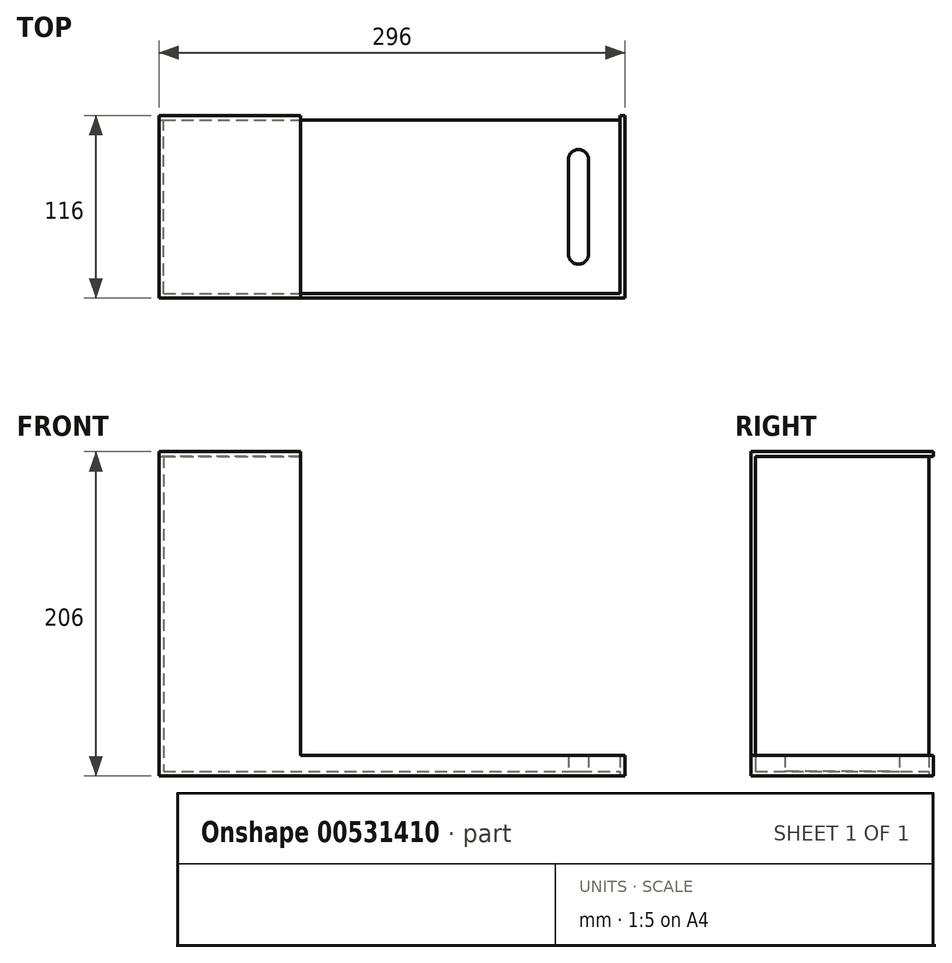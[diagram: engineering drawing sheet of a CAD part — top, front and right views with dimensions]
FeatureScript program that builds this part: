
annotation { "Feature Type Name" : "Feature", "Feature Type Description" : "" }
export const myFeature = defineFeature(function(context is Context, id is Id, definition is map)
    precondition{}
    {
        {
            var Q0;
            Q0=qCreatedBy(makeId("Front.planeOp"),FACE);
            var sketch = newSketch(context, id + "F0", { "sketchPlane" : qUnion([Q0])});
            skLineSegment(sketch, "E0", {"start": v(-49.76, 0) * mm, "end": v(-49.76, 203) * mm});
            skLineSegment(sketch, "E1", {"start": v(-49.76, 203) * mm, "end": v(-46.76, 203) * mm});
            skLineSegment(sketch, "E2", {"start": v(-46.76, 203) * mm, "end": v(-46.76, 3) * mm});
            skLineSegment(sketch, "E3", {"start": v(-46.76, 3) * mm, "end": v(243.24, 3) * mm});
            skLineSegment(sketch, "E4", {"start": v(243.24, 3) * mm, "end": v(243.24, 0) * mm});
            skLineSegment(sketch, "E5", {"start": v(243.24, 0) * mm, "end": v(-49.76, 0) * mm});
            skSolve(sketch);
        }
        {
            var Q0;
            Q0 = qSketchRegion(id + "F0", true);
            extrude(context, id + "F1", {"entities" : qUnion([Q0]), "depth" : 55 * mm, "offsetDistance" : 25 * mm, "hasSecondDirection" : true, "secondDirectionOppositeDirection" : true, "secondDirectionDepth" : 55 * mm});
        }
        {
            var Q0;
            Q0=makeQuery(id+"F1.opExtrude","CAP_FACE",FACE,{"disambiguationData":[OSD([sQuery(id+"F0.wireOp",EDGE,"E0"),sQuery(id+"F0.wireOp",EDGE,"E1"),sQuery(id+"F0.wireOp",EDGE,"E2"),sQuery(id+"F0.wireOp",EDGE,"E3"),sQuery(id+"F0.wireOp",EDGE,"E4"),sQuery(id+"F0.wireOp",EDGE,"E5")])],"isStart":false});
            cPlane(context, id + "F2", {"entities" : qUnion([Q0]), "cplaneType" : CPlaneType.OFFSET, "offset" : 0 * mm, "width" : 150 * mm, "height" : 150 * mm});
        }
        {
            var Q0;
            Q0=qCreatedBy(id+"F2.planeOp",FACE);
            var sketch = newSketch(context, id + "F3", { "sketchPlane" : qUnion([Q0])});
            skLineSegment(sketch, "E6.0", {"start": v(-49.76, 0) * mm, "end": v(-49.76, 203) * mm, "construction": true});
            skLineSegment(sketch, "E7.0", {"start": v(243.24, 0) * mm, "end": v(-49.76, 0) * mm, "construction": true});
            skLineSegment(sketch, "E8.bottom", {"start": v(-49.76, 203) * mm, "end": v(40.24, 203) * mm});
            skLineSegment(sketch, "E8.top", {"start": v(-49.76, 0) * mm, "end": v(243.24, 0) * mm});
            skLineSegment(sketch, "E8.left", {"start": v(-49.76, 203) * mm, "end": v(-49.76, 0) * mm});
            skLineSegment(sketch, "E8.right", {"start": v(243.24, 13) * mm, "end": v(243.24, 0) * mm});
            skLineSegment(sketch, "E9", {"start": v(40.24, 203) * mm, "end": v(40.24, 13) * mm});
            skLineSegment(sketch, "E10", {"start": v(40.24, 13) * mm, "end": v(243.24, 13) * mm});
            skSolve(sketch);
        }
        {
            var Q0;
            Q0 = qSketchRegion(id + "F3", true);
            extrude(context, id + "F4", {"entities" : qUnion([Q0]), "operationType" : NewBodyOperationType.ADD, "depth" : 3 * mm, "offsetDistance" : 25 * mm});
        }
        {
            var Q0;
            {var subQ0=sQuery(id+"F3.wireOp",EDGE,"E8.bottom");Q0=makeQuery(id+"FY8N2gA1KWKEWoe_1.1.F4.boolean.opBoolean","MERGE",FACE,{"derivedFrom":[makeQuery(id+"F4.boolean.opBoolean","MERGE",FACE,{"derivedFrom":[makeQuery(id+"F1.opExtrude","SWEPT_FACE",FACE,{"disambiguationData":[OSD([sQuery(id+"F0.wireOp",EDGE,"E1")])]}),makeQuery(id+"F4.opExtrude","SWEPT_FACE",FACE,{"disambiguationData":[OSD([subQ0])]})]}),makeQuery(id+"FY8N2gA1KWKEWoe_1.1.F4.opExtrude","SWEPT_FACE",FACE,{"disambiguationData":[OSD([subQ0])]})]});}
            cPlane(context, id + "F5", {"entities" : qUnion([Q0]), "cplaneType" : CPlaneType.OFFSET, "offset" : 0 * mm, "width" : 150 * mm, "height" : 150 * mm});
        }
        {
            var Q0;
            Q0=qCreatedBy(id+"F5.planeOp",FACE);
            var sketch = newSketch(context, id + "F6", { "sketchPlane" : qUnion([Q0])});
            skLineSegment(sketch, "E11.0", {"start": v(-49.76, 58) * mm, "end": v(40.24, 58) * mm, "construction": true});
            skLineSegment(sketch, "E12.0", {"start": v(-49.76, -58) * mm, "end": v(-49.76, 58) * mm, "construction": true});
            skLineSegment(sketch, "E13.bottom", {"start": v(40.24, 58) * mm, "end": v(-49.76, 58) * mm});
            skLineSegment(sketch, "E13.top", {"start": v(40.24, -58) * mm, "end": v(-49.76, -58) * mm});
            skLineSegment(sketch, "E13.left", {"start": v(40.24, 58) * mm, "end": v(40.24, -58) * mm});
            skLineSegment(sketch, "E13.right", {"start": v(-49.76, 58) * mm, "end": v(-49.76, -58) * mm});
            skSolve(sketch);
        }
        {
            var Q0;
            Q0 = qSketchRegion(id + "F6", true);
            extrude(context, id + "F7", {"entities" : qUnion([Q0]), "operationType" : NewBodyOperationType.ADD, "depth" : 3 * mm, "offsetDistance" : 25 * mm});
        }
        {
            var Q0;
            {var subQ0=sQuery(id+"F3.wireOp",EDGE,"E8.right");Q0=makeQuery(id+"FY8N2gA1KWKEWoe_1.1.F4.boolean.opBoolean","MERGE",FACE,{"derivedFrom":[makeQuery(id+"F4.boolean.opBoolean","MERGE",FACE,{"derivedFrom":[makeQuery(id+"F1.opExtrude","SWEPT_FACE",FACE,{"disambiguationData":[OSD([sQuery(id+"F0.wireOp",EDGE,"E4")])]}),makeQuery(id+"F4.opExtrude","SWEPT_FACE",FACE,{"disambiguationData":[OSD([subQ0])]})]}),makeQuery(id+"FY8N2gA1KWKEWoe_1.1.F4.opExtrude","SWEPT_FACE",FACE,{"disambiguationData":[OSD([subQ0])]})]});}
            cPlane(context, id + "F8", {"entities" : qUnion([Q0]), "cplaneType" : CPlaneType.OFFSET, "offset" : 0 * mm, "width" : 150 * mm, "height" : 150 * mm});
        }
        {
            var Q0;
            Q0=qCreatedBy(id+"F8.planeOp",FACE);
            var sketch = newSketch(context, id + "F9", { "sketchPlane" : qUnion([Q0])});
            skLineSegment(sketch, "E14.0", {"start": v(-58, 13) * mm, "end": v(-58, 0) * mm, "construction": true});
            skLineSegment(sketch, "E15.0", {"start": v(-58, 0) * mm, "end": v(58, 0) * mm, "construction": true});
            skLineSegment(sketch, "E16.bottom", {"start": v(-58, 13) * mm, "end": v(58, 13) * mm});
            skLineSegment(sketch, "E16.top", {"start": v(-58, 0) * mm, "end": v(58, 0) * mm});
            skLineSegment(sketch, "E16.left", {"start": v(-58, 13) * mm, "end": v(-58, 0) * mm});
            skLineSegment(sketch, "E16.right", {"start": v(58, 13) * mm, "end": v(58, 0) * mm});
            skSolve(sketch);
        }
        {
            var Q0;
            Q0 = qSketchRegion(id + "F9", true);
            extrude(context, id + "F10", {"entities" : qUnion([Q0]), "operationType" : NewBodyOperationType.ADD, "depth" : 3 * mm, "offsetDistance" : 25 * mm});
        }
        {
            var Q0;
            Q0=makeQuery(id+"F1.opExtrude","SWEPT_FACE",FACE,{"disambiguationData":[OSD([sQuery(id+"F0.wireOp",EDGE,"E3")])]});
            cPlane(context, id + "F11", {"entities" : qUnion([Q0]), "cplaneType" : CPlaneType.OFFSET, "offset" : 0 * mm, "width" : 150 * mm, "height" : 150 * mm});
        }
        {
            var Q0;
            Q0=qCreatedBy(id+"F11.planeOp",FACE);
            var sketch = newSketch(context, id + "F12", { "sketchPlane" : qUnion([Q0])});
            skLineSegment(sketch, "E17", {"start": v(210.31, 0) * mm, "end": v(210.31, -29.91) * mm});
            skLineSegment(sketch, "E18", {"start": v(223.24, 0) * mm, "end": v(223.24, -29.91) * mm});
            skArc(sketch, "E19", {"start": v(210.31, -29.91) * mm, "mid": v(216.77, -36.37) * mm, "end": v(223.24, -29.91) * mm});
            skLineSegment(sketch, "E20.MirrorCS", {"start": v(210.31, 0) * mm, "end": v(210.31, 29.91) * mm});
            skLineSegment(sketch, "E21.MirrorCS", {"start": v(223.24, 0) * mm, "end": v(223.24, 29.91) * mm});
            skArc(sketch, "E22.MirrorCS", {"start": v(210.31, 29.91) * mm, "mid": v(216.77, 36.37) * mm, "end": v(223.24, 29.91) * mm});
            skLineSegment(sketch, "E23.0", {"start": v(243.24, -55) * mm, "end": v(243.24, 55) * mm, "construction": true});
            skSolve(sketch);
        }
        {
            var Q0;
            Q0 = qSketchRegion(id + "F12", true);
            extrude(context, id + "F13", {"entities" : qUnion([Q0]), "operationType" : NewBodyOperationType.ADD, "depth" : 10 * mm, "offsetDistance" : 25 * mm});
        }
    });
